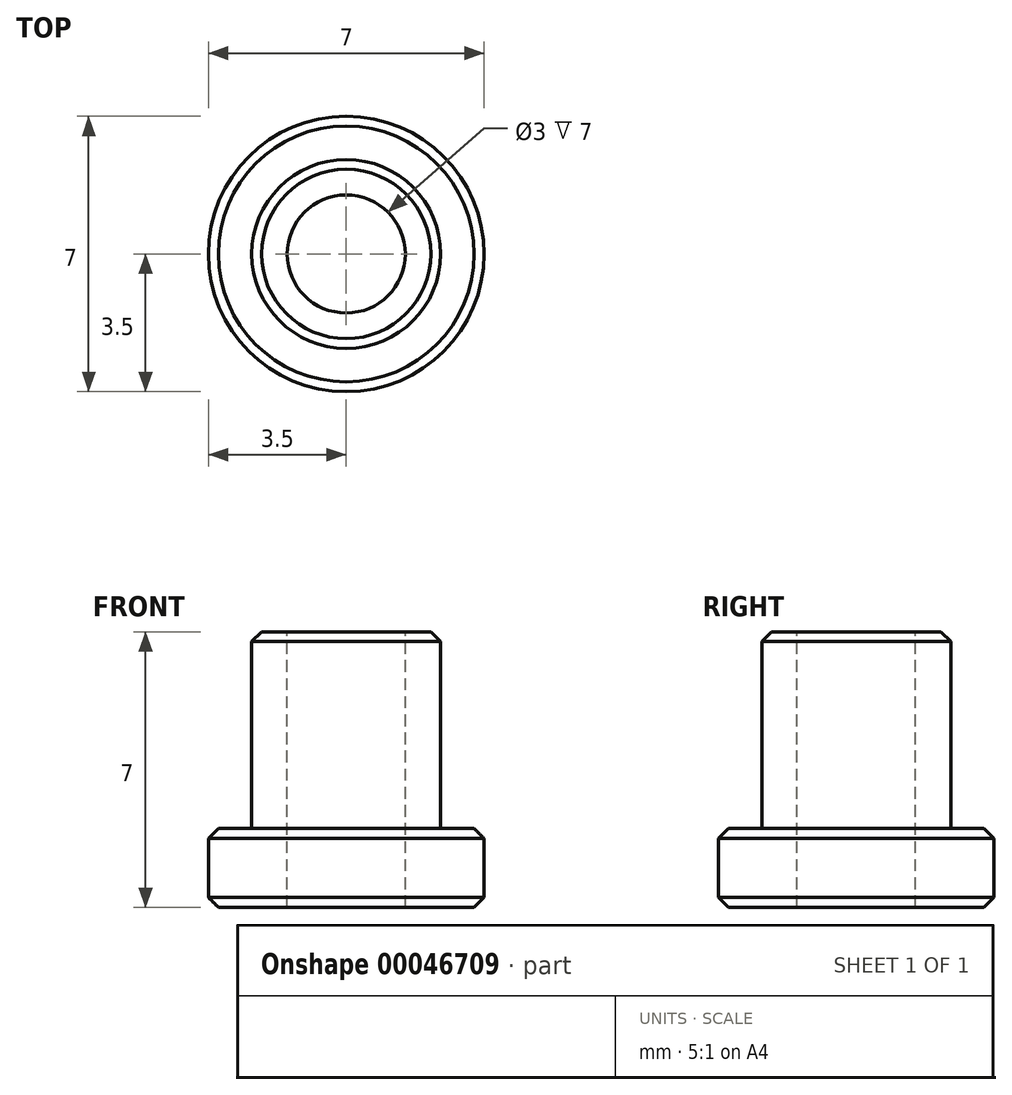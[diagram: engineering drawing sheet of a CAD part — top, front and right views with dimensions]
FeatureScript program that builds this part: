
annotation { "Feature Type Name" : "Feature", "Feature Type Description" : "" }
export const myFeature = defineFeature(function(context is Context, id is Id, definition is map)
    precondition{}
    {
        {
            var Q0;
            Q0=qCreatedBy(makeId("Right.planeOp"),FACE);
            var sketch = newSketch(context, id + "F0", { "sketchPlane" : qUnion([Q0])});
            skLineSegment(sketch, "E0", {"start": v(-1.5, 7) * mm, "end": v(-2.4, 7) * mm});
            skLineSegment(sketch, "E1", {"start": v(-2.4, 7) * mm, "end": v(-2.4, 2) * mm});
            skLineSegment(sketch, "E2", {"start": v(-2.4, 2) * mm, "end": v(-3.5, 2) * mm});
            skLineSegment(sketch, "E3", {"start": v(-3.5, 2) * mm, "end": v(-3.5, 0) * mm});
            skLineSegment(sketch, "E4", {"start": v(-3.5, 0) * mm, "end": v(-1.5, 0) * mm});
            skLineSegment(sketch, "E5", {"start": v(-1.5, 0) * mm, "end": v(-1.5, 7) * mm});
            skLineSegment(sketch, "E6", {"start": v(0, 18.89) * mm, "end": v(0, -5.22) * mm, "construction": true});
            skSolve(sketch);
        }
        {
            var Q0;
            Q0=makeQuery(id+"F0.imprint","IMPRINT",FACE,{"disambiguationData":[TD([[makeQuery(id+"F0.imprint","IMPRINT",EDGE,{"derivedFrom":sQuery(id+"F0.wireOp",EDGE,"E0")}),1.0]])]});
            var Q1;
            Q1=sQuery(id+"F0.wireOp",EDGE,"E5");
            var Q2;
            Q2=sQuery(id+"F0.wireOp",EDGE,"E0");
            var Q3;
            Q3=sQuery(id+"F0.wireOp",EDGE,"E1");
            var Q4;
            Q4=sQuery(id+"F0.wireOp",EDGE,"E2");
            var Q5;
            Q5=sQuery(id+"F0.wireOp",EDGE,"E6");
            revolve(context, id + "F1", {"surfaceOperationType" : NewSurfaceOperationType.NEW, "entities" : qUnion([Q0]), "surfaceEntities" : qUnion([Q1, Q2, Q3, Q4]), "axis" : qUnion([Q5]), "revolveType" : RevolveType.FULL});
        }
        {
            var Q0;
            Q0=makeQuery(id+"F1.opRevolve","SWEPT_EDGE",EDGE,{"disambiguationData":[OSD([sQuery(id+"F0.wireOp",EDGE,"E0"),sQuery(id+"F0.wireOp",EDGE,"E1")])]});
            var Q1;
            Q1=makeQuery(id+"F1.opRevolve","SWEPT_EDGE",EDGE,{"disambiguationData":[OSD([sQuery(id+"F0.wireOp",EDGE,"E2"),sQuery(id+"F0.wireOp",EDGE,"E3")])]});
            var Q2;
            Q2=makeQuery(id+"F1.opRevolve","SWEPT_EDGE",EDGE,{"disambiguationData":[OSD([sQuery(id+"F0.wireOp",EDGE,"E3"),sQuery(id+"F0.wireOp",EDGE,"E4")])]});
            chamfer(context, id + "F2", {"entities" : qUnion([Q0, Q1, Q2]), "width" : 0.25 * mm, "tangentPropagation" : true});
        }
    });
